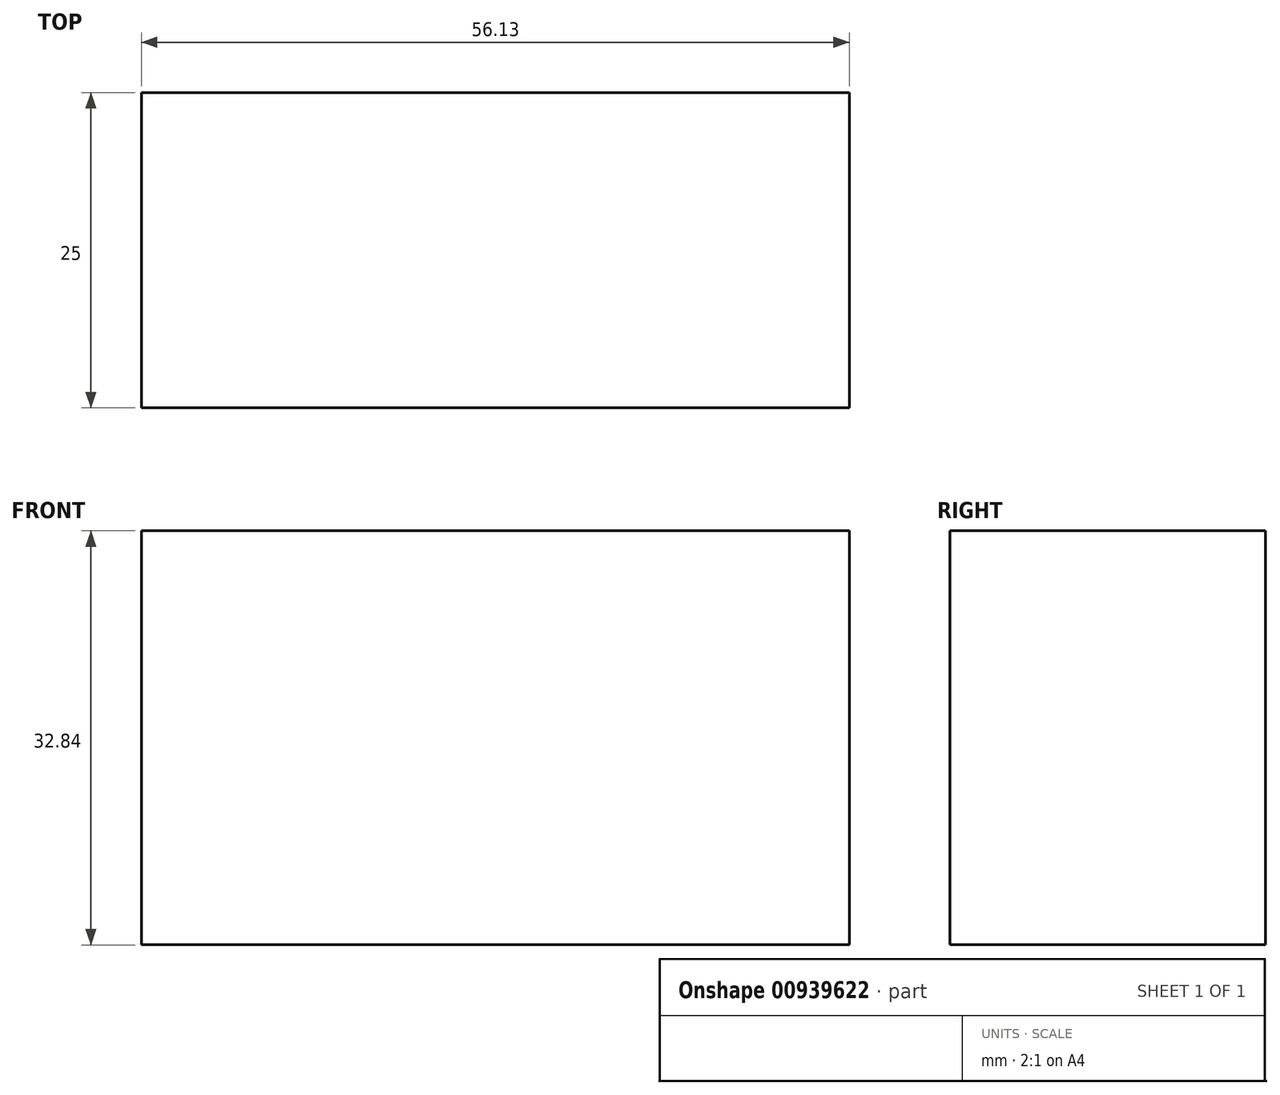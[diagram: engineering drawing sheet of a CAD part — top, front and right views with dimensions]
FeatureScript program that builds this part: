
annotation { "Feature Type Name" : "Feature", "Feature Type Description" : "" }
export const myFeature = defineFeature(function(context is Context, id is Id, definition is map)
    precondition{}
    {
        {
            var Q0;
            Q0=qCreatedBy(makeId("Front.planeOp"),FACE);
            var sketch = newSketch(context, id + "F0", { "sketchPlane" : qUnion([Q0])});
            skLineSegment(sketch, "E0.bottom", {"start": v(-59.13, 17.57) * mm, "end": v(-3, 17.57) * mm});
            skLineSegment(sketch, "E0.top", {"start": v(-59.13, -15.27) * mm, "end": v(-3, -15.27) * mm});
            skLineSegment(sketch, "E0.left", {"start": v(-59.13, 17.57) * mm, "end": v(-59.13, -15.27) * mm});
            skLineSegment(sketch, "E0.right", {"start": v(-3, 17.57) * mm, "end": v(-3, -15.27) * mm});
            skSolve(sketch);
        }
        {
            var Q0;
            Q0 = qSketchRegion(id + "F0", true);
            extrude(context, id + "F1", {"entities" : qUnion([Q0]), "depth" : 25 * mm, "offsetDistance" : 25 * mm});
        }
    });
